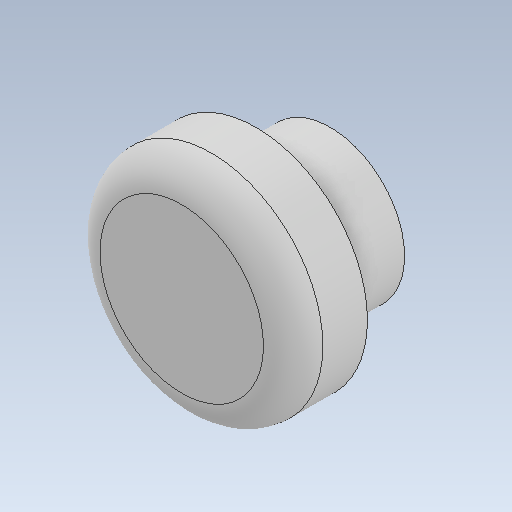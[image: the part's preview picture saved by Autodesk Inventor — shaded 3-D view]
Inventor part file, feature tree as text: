
AUTODESK INVENTOR PART (.ipt)
format: ipt  version: 2020 (Build 240168000, 168)  size: 149,504 bytes
history: native  units: mm
features: sketch x3, extrude x2, fillet x1, hole x1
ambient origin geometry x8: Origin, YZ Plane, XZ Plane, XY Plane, X Axis, Y Axis, Z Axis, Center Point
bodies: Solid1 (feature_tree)
feature tree (7):
  extrude  "Extrusion1"  Depth=10.0mm
  extrude  "Extrusion2"  Depth=5.0mm
  fillet  "Fillet1"  Radius=5.0mm
  hole  "Hole1"  [1 undecoded]
  sketch  "Sketch1"  dims[d0=4.8mm d1=10.0mm]
  sketch  "Sketch2"  dims[d2=5.0mm d3=0.0mm d4=15.0mm d5=5.0mm d6=0.0mm]
  sketch  "Sketch3"  dims[d7=2.0mm d8=2.5mm d9=2.5mm d10=6.0mm d11=10.0mm d12=2.0mm d13=90.0deg d14=8.0mm d15=20.594885mm]
note: 1 required parameter value undecoded (feature->parameter linkage not recoverable at this tier; creation-order binding heuristic only, values carry confidence <= 0.55)
